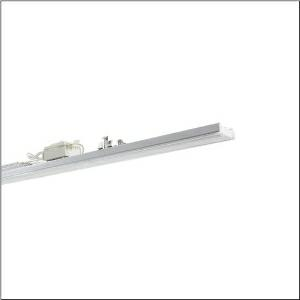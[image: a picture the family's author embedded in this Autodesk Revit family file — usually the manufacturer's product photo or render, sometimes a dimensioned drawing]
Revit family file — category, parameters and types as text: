
# Revit family: licross_11_recessed_extreme_ho_51tl12dn4exme
name_source: partatom
category: Lighting Fixtures
units: mm (PartAtom-declared; Revit-internal decimal feet)

## family parameters
Cut with Voids When Loaded = No
Host = Face
Light Source = No
Part Type = Normal
Room Calculation Point = No
Round Connector Dimension = Use Diameter
Shared = No

## types (1)
- --- (1 x LED, 14030 lm, 76.8 W, 4000K)
    Apparent Load = 77 VA
    CIE Flux Codes = 66 91 98 100 100
    Color Rendering = 80
    Color Temperature = 4000K
    Default Elevation = 1800 mm
    Description = Licross 11 Recessed extreme HO, luminaire insert, of sheet steel, coil coated, white, length: 1.500mm, width: 66mm, height: 67mm, LED rated luminous flux: 14.030lm, light colour: 840, SDCM (Standard Deviation of Colour Matching)MacAdam ≤ 2 SDCM (initial), control gear: DALI 2, with plug, 5-pole, with phase selection, mains connection: 220..240V, AC, 50/60Hz, rated input power: 77W, internal wiring halogen-free, primary optical cover: cover, of PMMA, light emission: direct distribution, primary light characteristic: symmetric, protection rating (complete): IP40, insulation class (complete): insulation class I (protective earthing), certification: CE, ENEC, VDE, UKCA, protection symbol: D if used in an environment without relevant dust loads with corresponding accessories, impact resistance: IK06, permissible ambient temperature for indoor applications: -40..+40°C, corresponds to IFS (International Featured Standards) requirements for safety and quality in the food industry, reducing of maximum allowable ambient temperature of 5°C with ceiling mounting, LABS conformity tested according to VDMA 24364:2018-05, The light source and the operating device comply with the requirements of the Ecodesign Regulation (EU) 2019/2020 and are replaceable in accordance with this regulation, packaging unit: 1 piece
    Height = 58 mm
    Lamp = 1 x LED
    Lamp Light Flux = 14030 lm
    Lamp Power = 76.8 W
    Lamp count = 1
    Length = 1500 mm
    Luminous efficacy = 183 lm/W
    Manufacturer = Siteco
    ModVariant = No
    Model = 51TL12DN4EXME
    Mounting Place = Ceiling
    Mounting Type = Pendant
    Number of Poles = 1
    OnlyDefault = Yes
    Power Factor = 1
    Product Name = Licross 11 Recessed extreme HO
    Product group = luminaire insert | ceiling pendant
    ProductGroupID = 901
    Protection Class = Protection class I
    Protection Degree = IP 40
    RLX_Detail_Level = 1
    RLX_Emergency_Light_Flux = 0 lm
    RLX_Emergency_Type = 0
    RLX_Emergency_Type_DB = No
    RlxData = <blob elided: 24865 chars, md5=f0cfe5a4>
    Socket = socket
    Standby Power = 0 W
    System Light Flux = 14030 lm
    System Power = 77 W
    Type Comments = factory setting: luminous flux: 100 % | dim-lin: 254 | 522 mA
    Type Image = l_1296930.jpg
    URL = http://relux.com
    VarID = @adj_087449
    Voltage = 0 V
    Weight = 0.00 kg
    Width = 66 mm

## geometry (parser evidence)
native form markers: Blend x4, Sweep x12
no freeform markers — native parametric forms only
